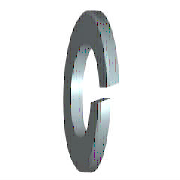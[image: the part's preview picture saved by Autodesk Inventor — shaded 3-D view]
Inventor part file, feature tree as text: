
AUTODESK INVENTOR PART (.ipt)
format: ipt  version: 2021 (Build 250183000, 183)  size: 123,904 bytes
history: native  units: mm (DEFAULTED — no unit token found)
features: sketch x2, extrude x1, other x1, plane x1
ambient origin geometry x6: Origin, YZ Plane, X Axis, Y Axis, Z Axis, Center Point
bodies: Solid1 (feature_tree), Body (feature_tree)
feature tree (5):
  extrude  "Cut"  Depth=41.0mm
  other  "Work Axis1"
  plane  "Work Plane1"
  sketch  "Sketch1"  dims[d0=21.0mm d1=41.0mm]
  sketch  "Sketch2"  dims[d2=6.0mm d3=0.0mm d4=1.2mm d5=1.2mm d6=90.0deg d7=6.0mm d8=0.0mm d9=0.0mm d10=0.0mm d11=0.0mm d12=0.0mm]
